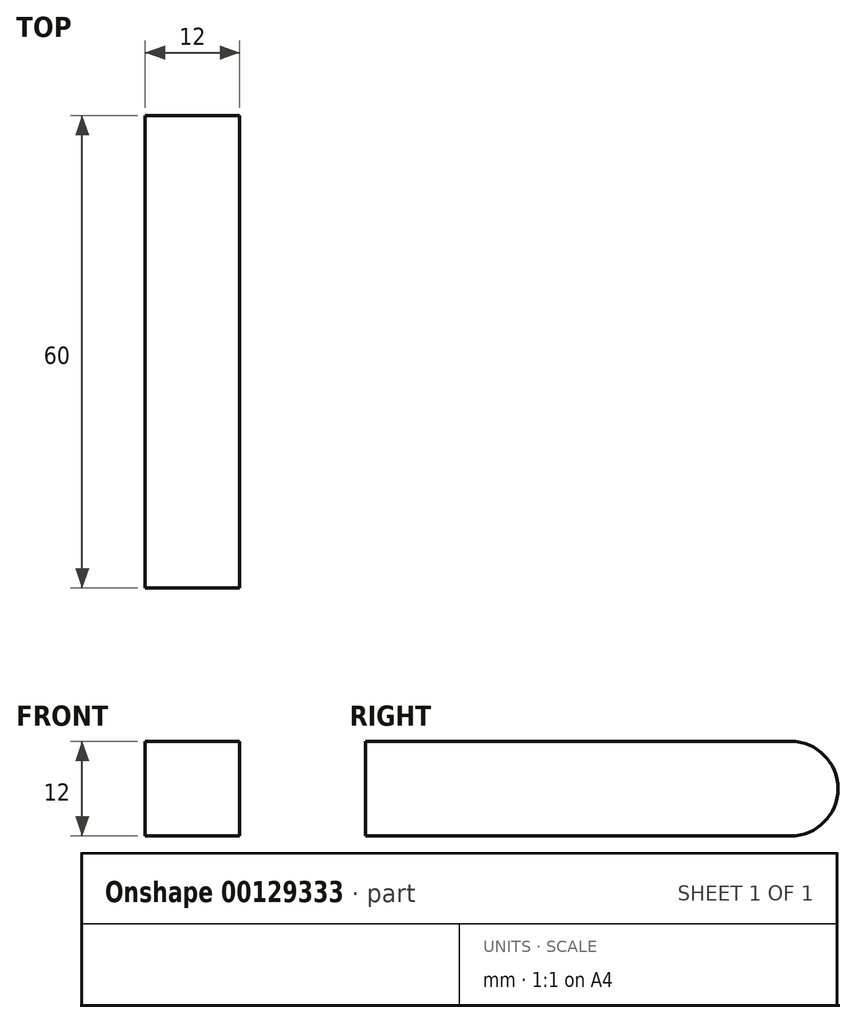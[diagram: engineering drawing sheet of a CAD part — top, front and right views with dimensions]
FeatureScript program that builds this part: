
annotation { "Feature Type Name" : "Feature", "Feature Type Description" : "" }
export const myFeature = defineFeature(function(context is Context, id is Id, definition is map)
    precondition{}
    {
        {
            var Q0;
            Q0=qCreatedBy(makeId("Right.planeOp"),FACE);
            var sketch = newSketch(context, id + "F0", { "sketchPlane" : qUnion([Q0])});
            skLineSegment(sketch, "E0.bottom", {"start": v(0, 0) * mm, "end": v(54, 0) * mm});
            skLineSegment(sketch, "E0.top", {"start": v(0, 12) * mm, "end": v(54, 12) * mm});
            skLineSegment(sketch, "E0.left", {"start": v(0, 0) * mm, "end": v(0, 12) * mm});
            skLineSegment(sketch, "E0.right", {"start": v(60, 6) * mm, "end": v(60, 6) * mm});
            skPoint(sketch, "E1.visualSharp", {"position": v(60, 12) * mm});
            skArc(sketch, "E1.filletArc", {"start": v(60, 6) * mm, "mid": v(58.24, 10.24) * mm, "end": v(54, 12) * mm});
            skPoint(sketch, "E2.visualSharp", {"position": v(60, 0) * mm});
            skArc(sketch, "E2.filletArc", {"start": v(54, 0) * mm, "mid": v(58.24, 1.76) * mm, "end": v(60, 6) * mm});
            skSolve(sketch);
        }
        {
            var Q0;
            Q0=makeQuery(id+"F0.imprint","IMPRINT",FACE,{"disambiguationData":[TD([[makeQuery(id+"F0.imprint","IMPRINT",EDGE,{"derivedFrom":sQuery(id+"F0.wireOp",EDGE,"E0.bottom")}),1.0]])]});
            extrude(context, id + "F1", {"entities" : qUnion([Q0]), "depth" : 12 * mm});
        }
    });
